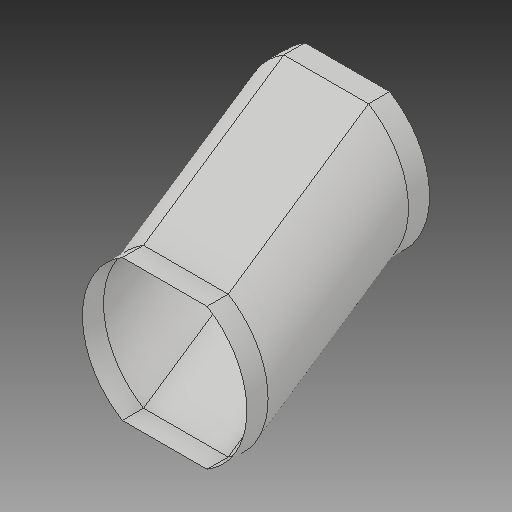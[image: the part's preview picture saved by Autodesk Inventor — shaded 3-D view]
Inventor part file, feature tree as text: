
AUTODESK INVENTOR PART (.ipt)
format: ipt  version: 2017 (Build 210142000, 142)  size: 151,040 bytes
history: native  units: in
note: dims shown in document units (in); Inventor stores cm internally (conversion verified against a paired STEP export)
features: sketch x2, extrude x2, plane x1, sweep x1, delete_face x1
ambient origin geometry x8: Origin, YZ Plane, XZ Plane, XY Plane, X Axis, Y Axis, Z Axis, Center Point
bodies: Solid1 (feature_tree)
feature tree (7):
  sketch  "Sketch1"  dims[d0=6.6667in d3=1.0in d4=0.0in d12=8.0in]
  extrude  "connection top"  Depth=8.0in
  plane  "Work Plane2"
  sweep  "ramp"
  extrude  "connection bottom"  Depth=3.8873in TaperAngle=0.0deg
  delete_face  "Delete Face1"
  sketch  "Sketch6"  dims[d28=8.0in d45=0.0in d46=0.0in d49=1.0in d50=0.0in d70=0.8521in d87=4.0in d89=3.8873in d90=3.8873in d94=1.6458in d100=3.3333in d102=4.0in d104=3.8873in d105=3.8873in d109=1.6458in d115=3.3333in]
